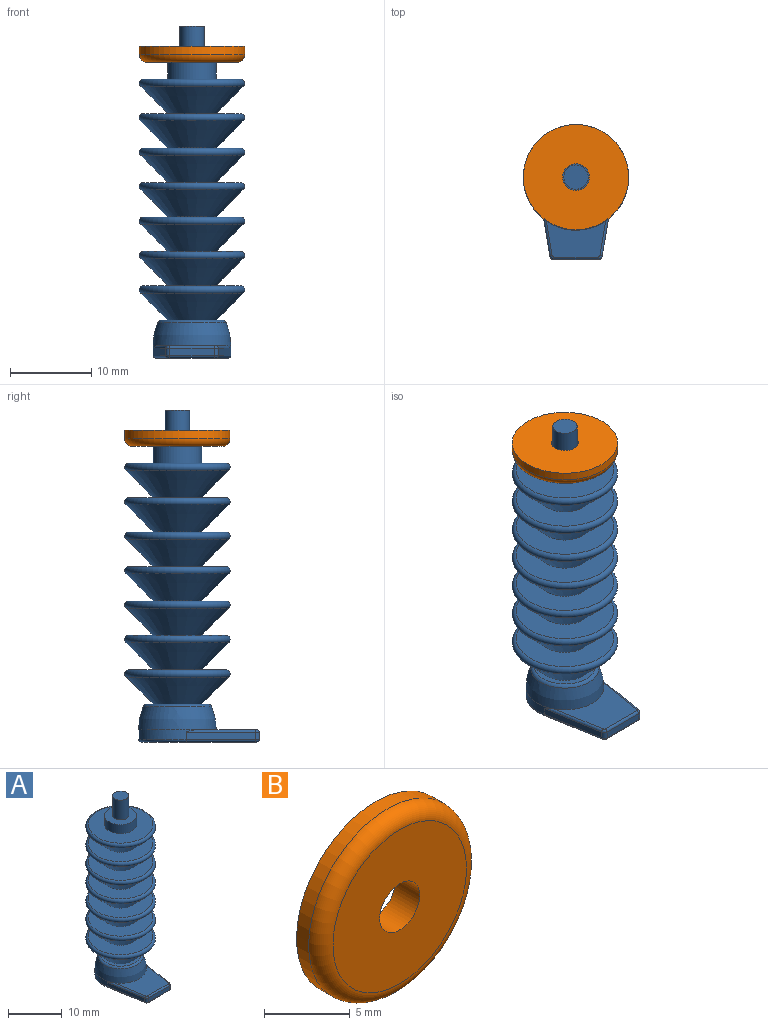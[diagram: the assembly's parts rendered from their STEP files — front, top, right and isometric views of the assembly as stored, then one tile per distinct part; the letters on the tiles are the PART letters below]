
ASSEMBLY  parts=2 mates=1
PART A: 53 faces, bbox 14.1x17.1x41 mm
  f0: revolved ~9.59x9.59mm, area 85.4mm2, adj f31,f34,f38
  f1: plane 7.51x7.51mm, normal (0,0,1), area 16mm2, adj f29,f31
  f2: cylinder r=3mm len=6mm, axis (0,0,-1), area 39.1mm2, adj f3,f30
  f3: plane 12.06x12.06mm, normal (0,0,1), area 86mm2, adj f2,f4
  f4: torus R=6mm, axis (0,0,-1), area 48.5mm2, adj f3,f5
  f5: cone r=3mm half-angle=44.8deg, axis (0,0,1), area 137.1mm2, adj f4,f6
  f6: cylinder r=3mm len=6mm, axis (0,0,-1), area 0.5mm2, adj f5,f7
  f7: plane 12.06x12.06mm, normal (0,0,1), area 86mm2, adj f6,f8
  f8: torus R=6mm, axis (0,0,-1), area 48.5mm2, adj f7,f9
  f9: cone r=3mm half-angle=44.8deg, axis (0,0,1), area 137.1mm2, adj f8,f10
  f10: cylinder r=3mm len=6mm, axis (0,0,-1), area 0.5mm2, adj f9,f11
  f11: plane 12.06x12.06mm, normal (0,0,1), area 86mm2, adj f10,f12
  f12: torus R=6mm, axis (0,0,-1), area 48.5mm2, adj f11,f13
  f13: cone r=3mm half-angle=44.8deg, axis (0,0,1), area 137.1mm2, adj f12,f14
  f14: cylinder r=3mm len=6mm, axis (0,0,-1), area 0.5mm2, adj f13,f15
  f15: plane 12.06x12.06mm, normal (0,0,1), area 86mm2, adj f14,f16
  f16: torus R=6mm, axis (0,0,-1), area 48.5mm2, adj f15,f17
  f17: cone r=3mm half-angle=44.8deg, axis (0,0,1), area 137.1mm2, adj f16,f18
  f18: cylinder r=3mm len=6mm, axis (0,0,-1), area 0.5mm2, adj f17,f19
  f19: plane 12.06x12.06mm, normal (0,0,1), area 86mm2, adj f18,f20
  f20: torus R=6mm, axis (0,0,-1), area 48.5mm2, adj f19,f21
  f21: cone r=3mm half-angle=44.8deg, axis (0,0,1), area 137.1mm2, adj f20,f22
  f22: cylinder r=3mm len=6mm, axis (0,0,-1), area 0.5mm2, adj f21,f23
  f23: plane 12.06x12.06mm, normal (0,0,1), area 86mm2, adj f22,f24
  f24: torus R=6mm, axis (0,0,-1), area 48.5mm2, adj f23,f25
  f25: cone r=3mm half-angle=44.8deg, axis (0,0,1), area 137.1mm2, adj f24,f26
  f26: cylinder r=3mm len=6mm, axis (0,0,-1), area 0.5mm2, adj f25,f27
  f27: plane 12.06x12.06mm, normal (0,0,1), area 86mm2, adj f26,f28
  f28: torus R=6mm, axis (0,0,-1), area 48.5mm2, adj f27,f29
  f29: cone r=3mm half-angle=44.8deg, axis (0,0,1), area 137.1mm2, adj f1,f28
  f30: plane 6x6mm, normal (0,0,1), area 21.2mm2, adj f2,f32
  f31: torus R=3.75mm, axis (0,0,-1), area 14.6mm2, adj f0,f1
  f32: cylinder r=1.5mm len=4.5mm, axis (0,0,-1), area 42.4mm2, adj f30,f33
  f33: plane 3x3mm, normal (0,0,1), area 7.1mm2, adj f32
  f34: plane 8.36x7.44mm, normal (0,0,1), area 38.2mm2, adj f0,f42,f43,f44,f45,f46
  f35: plane 5.5x0.9mm, normal (0,-1,0), area 5mm2, adj f36,f40,f44,f49
  f36: cylinder r=0.5mm len=0.9mm, axis (0,0,1), area 0.7mm2, adj f35,f37,f43,f47
  f37: plane 8.56x1.43mm, normal (-0.99,-0.16,0), area 7.8mm2, adj f36,f38,f42,f48
  f38: cylinder r=4.8mm len=9.6mm, axis (0,0,1), area 21.2mm2, adj f0,f37,f39,f42,f46,f50
  f39: plane 8.56x1.43mm, normal (0.99,-0.16,0), area 7.8mm2, adj f38,f40,f46,f52
  f40: cylinder r=0.5mm len=0.9mm, axis (0,0,1), area 0.7mm2, adj f35,f39,f45,f51
  f41: plane 14.3x9mm, normal (0,0,-1), area 105mm2, adj f47,f48,f49,f50,f51,f52
  f42: cylinder r=0.3mm len=8.62mm, axis (-0.16,0.99,0), area 3.8mm2, adj f34,f37,f38,f43
  f43: torus R=0.2mm, axis (0,0,-1), area 0.3mm2, adj f34,f36,f42,f44
  f44: cylinder r=0.3mm len=5.5mm, axis (-1,0,0), area 2.6mm2, adj f34,f35,f43,f45
  f45: torus R=0.2mm, axis (0,0,-1), area 0.3mm2, adj f34,f40,f44,f46
  f46: cylinder r=0.3mm len=8.62mm, axis (-0.16,-0.99,0), area 3.8mm2, adj f34,f38,f39,f45
  f47: torus R=0.2mm, axis (0,0,-1), area 0.3mm2, adj f36,f41,f48,f49
  f48: cylinder r=0.3mm len=8.63mm, axis (0.16,-0.99,0), area 4.1mm2, adj f37,f41,f47,f50
  f49: cylinder r=0.3mm len=5.5mm, axis (1,0,0), area 2.6mm2, adj f35,f41,f47,f51
  f50: torus R=4.5mm, axis (0,0,-1), area 8mm2, adj f38,f41,f48,f52
  f51: torus R=0.2mm, axis (0,0,-1), area 0.3mm2, adj f40,f41,f49,f52
  f52: cylinder r=0.3mm len=8.63mm, axis (0.16,0.99,0), area 4.1mm2, adj f39,f41,f50,f51
PART B: 5 faces, bbox 14.1x2x14.1 mm
  f0: cylinder r=1.65mm len=3.3mm, axis (0,1,0), area 20.7mm2, adj f2,f3
  f1: cylinder r=6.5mm len=13mm, axis (0,1,0), area 40.8mm2, adj f3,f4
  f2: plane 11x11mm, normal (0,-1,0), area 86.5mm2, adj f0,f4
  f3: plane 13x13mm, normal (0,1,0), area 124.2mm2, adj f0,f1
  f4: torus R=5.5mm, axis (0,-1,0), area 60.6mm2, adj f1,f2
PLACE A t=(-0.94,1.98,-17.65)mm
PLACE B rot(axis=(1,0,0),90deg) t=(-0.94,1.98,19.33)mm
MATE fastened B.f0 <-> A.f2  axis (0,0,-1) through (-0.94,1.98,17.33)mm
